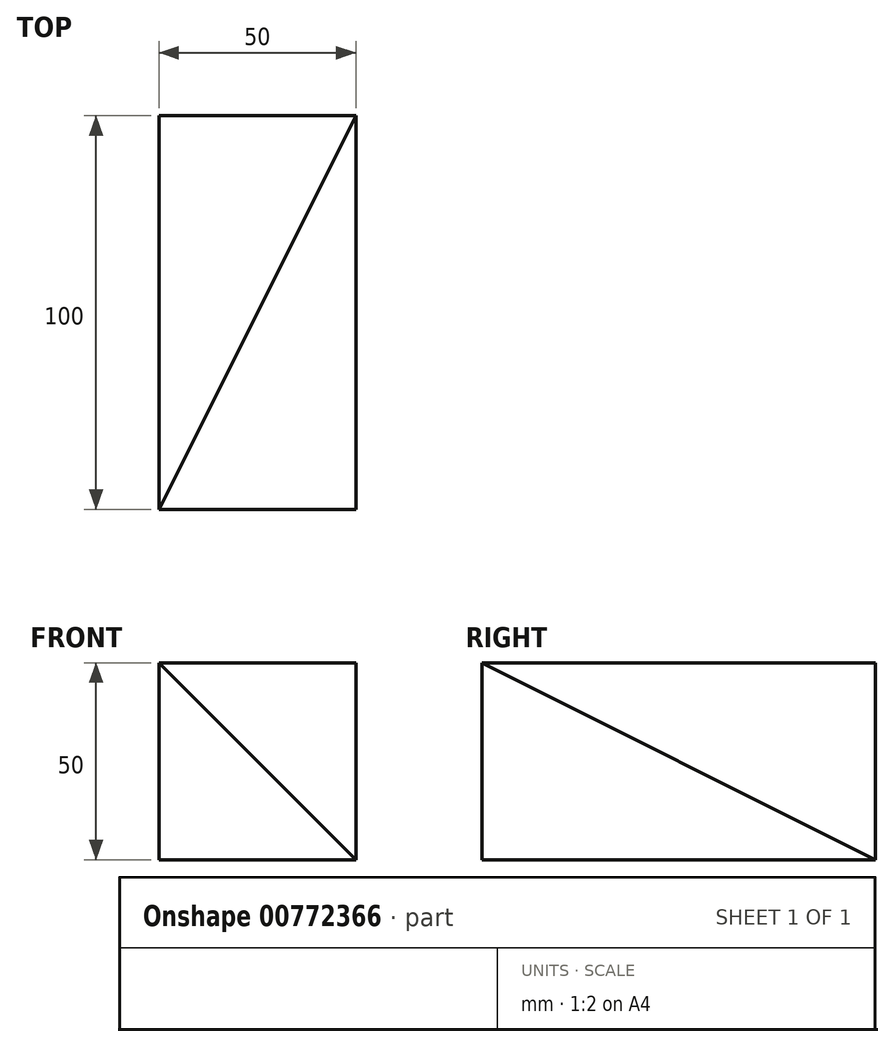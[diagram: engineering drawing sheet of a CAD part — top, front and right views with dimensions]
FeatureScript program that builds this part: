
annotation { "Feature Type Name" : "Feature", "Feature Type Description" : "" }
export const myFeature = defineFeature(function(context is Context, id is Id, definition is map)
    precondition{}
    {
        {
            var Q0;
            Q0=qCreatedBy(makeId("Front.planeOp"),FACE);
            var sketch = newSketch(context, id + "F0", { "sketchPlane" : qUnion([Q0])});
            skLineSegment(sketch, "E0", {"start": v(0, 0) * mm, "end": v(0, 50) * mm});
            skLineSegment(sketch, "E1", {"start": v(0, 50) * mm, "end": v(50, 0) * mm});
            skLineSegment(sketch, "E2", {"start": v(50, 0) * mm, "end": v(0, 0) * mm});
            skSolve(sketch);
        }
        {
            var Q0;
            Q0 = qSketchRegion(id + "F0", true);
            extrude(context, id + "F1", {"entities" : qUnion([Q0]), "oppositeDirection" : true, "depth" : 100 * mm, "offsetDistance" : 25 * mm});
        }
        {
            var Q0;
            Q0=makeQuery(id+"F1.opExtrude","SWEPT_FACE",FACE,{"disambiguationData":[OSD([sQuery(id+"F0.wireOp",EDGE,"E2")])]});
            var sketch = newSketch(context, id + "F2", { "sketchPlane" : qUnion([Q0])});
            skLineSegment(sketch, "E3", {"start": v(0, 0) * mm, "end": v(50, -100) * mm});
            skLineSegment(sketch, "E4", {"start": v(50, -100) * mm, "end": v(0, -100) * mm});
            skLineSegment(sketch, "E5", {"start": v(0, -100) * mm, "end": v(0, 0) * mm});
            skSolve(sketch);
        }
        {
            var Q0;
            Q0 = qSketchRegion(id + "F2", true);
            var Q1;
            Q1=makeQuery(id+"F1.opExtrude","CAP_VERTEX",VERTEX,{"disambiguationData":[OSD([sQuery(id+"F0.wireOp",EDGE,"E0"),sQuery(id+"F0.wireOp",EDGE,"E1")])],"isStart":true});
            extrude(context, id + "F3", {"entities" : qUnion([Q0]), "operationType" : NewBodyOperationType.ADD, "endBound" : BoundingType.UP_TO_VERTEX, "oppositeDirection" : true, "depth" : 50 * mm, "endBoundEntityVertex" : qUnion([Q1]), "offsetDistance" : 25 * mm});
        }
    });
